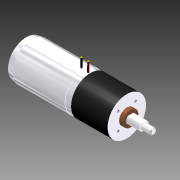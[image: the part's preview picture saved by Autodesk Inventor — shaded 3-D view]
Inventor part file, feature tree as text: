
AUTODESK INVENTOR PART (.ipt)
format: ipt  version: 2011 (Build 150239000, 239)  size: 153,088 bytes
history: native  units: mm (DEFAULTED — no unit token found)
features: sketch x8, extrude x7, projected_geometry x6, other x4, chamfer x2, plane x2, hole x1
ambient origin geometry x8: Origin, YZ Plane, XZ Plane, XY Plane, X Axis, Y Axis, Z Axis, Center Point
bodies: Solid1 (feature_tree)
feature tree (30):
  extrude  "Extrusion1"  Depth=60.0mm TaperAngle=0.0deg
  extrude  "Extrusion2"  Depth=40.0mm
  extrude  "Extrusion3"  Depth=16.0mm
  extrude  "Extrusion4"  Depth=9.5mm
  extrude  "Extrusion5"  Depth=4.75mm
  extrude  "Extrusion6"  Depth=3.75mm
  chamfer  "Chamfer1"  Distance=14.0mm
  chamfer  "Chamfer2"  Distance=6.5mm
  plane  "Work Plane1"
  plane  "Work Plane2"
  extrude  "Extrusion7"  Depth=10.0mm TaperAngle=0.0deg
  other  "Work Point1"
  other  "Work Point2"
  hole  "Hole1"  [1 undecoded]
  sketch  "Sketch1"  dims[d0=40.0mm d1=60.0mm d2=0.0mm]
  sketch  "Sketch2"  dims[d3=6.6mm d4=0.0mm d5=40.0mm]
  projected_geometry  "Projected Loop1"
  sketch  "Sketch3"  dims[d6=38.0mm d7=0.0mm d8=16.0mm]
  projected_geometry  "Projected Loop2"
  sketch  "Sketch4"  dims[d9=4.0mm d10=0.0mm d11=9.5mm]
  projected_geometry  "Projected Loop3"
  sketch  "Sketch5"  dims[d13=4.75mm d14=4.75mm]
  projected_geometry  "Projected Loop4"
  sketch  "Sketch6"  dims[d15=7.5mm d16=3.75mm]
  projected_geometry  "Projected Loop5"
  sketch  "Sketch8"  dims[d17=7.5mm]
  other  "Work Axis1"
  other  "Work Axis2"
  sketch  "Sketch9"  dims[d18=5.902433mm d19=14.0mm d20=0.0mm d21=6.5mm d22=10.0mm d23=0.0mm d24=1.0mm d25=2.0mm d26=45.0deg d27=1.0mm d28=2.0mm d29=13.962634mm d30=0.25mm d31=1.5mm d32=1.5mm d33=10.0mm d34=0.0mm d35=18.0mm d36=18.0mm d37=2.487mm d38=6.0mm d39=4.0mm d40=2.0mm d41=14.3117mm d42=8.0mm d43=20.594885mm]
  projected_geometry  "Projected Loop6"
note: 1 required parameter value undecoded (feature->parameter linkage not recoverable at this tier; creation-order binding heuristic only, values carry confidence <= 0.55)
